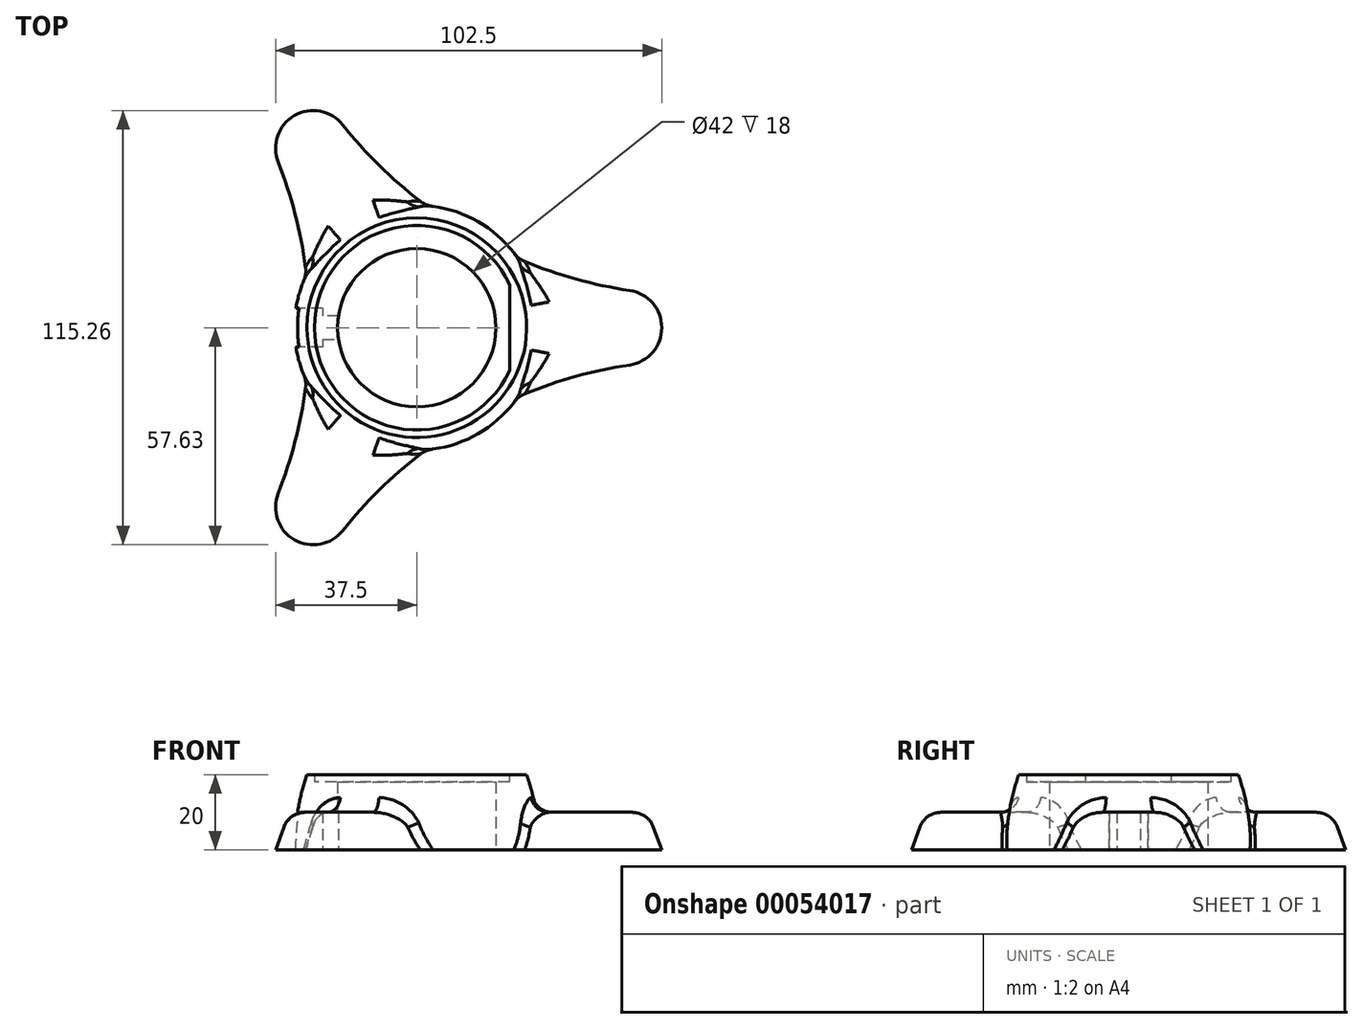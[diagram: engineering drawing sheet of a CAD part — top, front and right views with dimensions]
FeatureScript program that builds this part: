
annotation { "Feature Type Name" : "Feature", "Feature Type Description" : "" }
export const myFeature = defineFeature(function(context is Context, id is Id, definition is map)
    precondition{}
    {
        {
            var Q0;
            Q0=qCreatedBy(makeId("Front.planeOp"),FACE);
            var sketch = newSketch(context, id + "F0", { "sketchPlane" : qUnion([Q0])});
            skLineSegment(sketch, "E0", {"start": v(21, 0) * mm, "end": v(21, 18) * mm});
            skLineSegment(sketch, "E1", {"start": v(21, 18) * mm, "end": v(27.15, 18) * mm});
            skLineSegment(sketch, "E2", {"start": v(27.15, 18) * mm, "end": v(27.15, 20) * mm});
            skLineSegment(sketch, "E3", {"start": v(27.15, 20) * mm, "end": v(29.15, 20) * mm});
            skLineSegment(sketch, "E4", {"start": v(21, 0) * mm, "end": v(32.5, 0) * mm});
            skArc(sketch, "E5", {"start": v(32.5, 0) * mm, "mid": v(31.66, 10.14) * mm, "end": v(29.15, 20) * mm});
            skLineSegment(sketch, "E6", {"start": v(0, 0) * mm, "end": v(0, 24.17) * mm, "construction": true});
            skSolve(sketch);
        }
        {
            var Q0;
            Q0 = qSketchRegion(id + "F0", true);
            var Q1;
            Q1=sQuery(id+"F0.wireOp",EDGE,"E6");
            revolve(context, id + "F1", {"entities" : qUnion([Q0]), "axis" : qUnion([Q1]), "revolveType" : RevolveType.FULL});
        }
        {
            var Q0;
            Q0=qCreatedBy(makeId("Top.planeOp"),FACE);
            var sketch = newSketch(context, id + "F2", { "sketchPlane" : qUnion([Q0])});
            skLineSegment(sketch, "E7", {"start": v(0, 0) * mm, "end": v(55, 0) * mm, "construction": true});
            skLineSegment(sketch, "E8", {"start": v(0, 0) * mm, "end": v(-27.5, -47.63) * mm, "construction": true});
            skLineSegment(sketch, "E9", {"start": v(0, 0) * mm, "end": v(-27.5, 47.63) * mm, "construction": true});
            skArc(sketch, "E10", {"start": v(56.48, -9.89) * mm, "mid": v(65, 0) * mm, "end": v(56.48, 9.89) * mm});
            skArc(sketch, "E11", {"start": v(-36.8, -43.97) * mm, "mid": v(-32.5, -56.3) * mm, "end": v(-19.67, -53.86) * mm});
            skArc(sketch, "E12", {"start": v(-19.67, 53.86) * mm, "mid": v(-32.5, 56.3) * mm, "end": v(-36.8, 43.97) * mm});
            skArc(sketch, "E13", {"start": v(56.48, -9.89) * mm, "mid": v(14.23, -24.65) * mm, "end": v(-19.67, -53.86) * mm});
            skArc(sketch, "E14", {"start": v(-36.8, -43.97) * mm, "mid": v(-28.46, 0) * mm, "end": v(-36.8, 43.97) * mm});
            skArc(sketch, "E15", {"start": v(-19.67, 53.86) * mm, "mid": v(14.23, 24.65) * mm, "end": v(56.48, 9.89) * mm});
            skCircle(sketch, "E16", {"center": v(0, 0) * mm, "radius": 21 * mm});
            skSolve(sketch);
        }
        {
            var Q0;
            Q0 = qSketchRegion(id + "F2", true);
            extrude(context, id + "F3", {"entities" : qUnion([Q0]), "operationType" : NewBodyOperationType.ADD, "depth" : 10 * mm, "hasDraft" : true, "draftAngle" : 20 * degree, "draftPullDirection" : true});
        }
        {
            var Q0;
            {var subQ0=sQuery(id+"F2.wireOp",EDGE,"E13");var subQ1=sQuery(id+"F2.wireOp",EDGE,"E11");Q0=makeQuery(id+"F3.boolean.opBoolean","SPLIT",EDGE,{"disambiguationData":[TD([makeQuery(id+"F3.opExtrude","SWEPT_FACE",FACE,{"disambiguationData":[OSD([subQ1])]})])],"derivedFrom":makeQuery(id+"F3.opExtrude","CAP_EDGE",EDGE,{"disambiguationData":[OSD([subQ0])],"isStart":false})});}
            var Q1;
            {var subQ0=sQuery(id+"F2.wireOp",EDGE,"E10");var subQ1=sQuery(id+"F2.wireOp",EDGE,"E13");Q1=makeQuery(id+"F3.boolean.opBoolean","SPLIT",EDGE,{"disambiguationData":[TD([makeQuery(id+"F3.opExtrude","SWEPT_FACE",FACE,{"disambiguationData":[OSD([subQ0])]})])],"derivedFrom":makeQuery(id+"F3.opExtrude","CAP_EDGE",EDGE,{"disambiguationData":[OSD([subQ1])],"isStart":false})});}
            var Q2;
            Q2=makeQuery(id+"F3.opExtrude","CAP_EDGE",EDGE,{"disambiguationData":[OSD([sQuery(id+"F2.wireOp",EDGE,"E12")])],"isStart":false});
            fillet(context, id + "F4", {"entities" : qUnion([Q0, Q1, Q2]), "radius" : 6 * mm, "tangentPropagation" : true, "allowEdgeOverflow" : false});
        }
        {
            var Q0;
            Q0=makeQuery(id+"F1.opRevolve","SWEPT_FACE",FACE,{"disambiguationData":[OSD([sQuery(id+"F0.wireOp",EDGE,"E3")])]});
            var sketch = newSketch(context, id + "F5", { "sketchPlane" : qUnion([Q0])});
            skArc(sketch, "E17", {"start": v(24.65, -11.38) * mm, "mid": v(27.15, 0) * mm, "end": v(24.65, 11.38) * mm});
            skLineSegment(sketch, "E18", {"start": v(24.65, 11.38) * mm, "end": v(24.65, -11.38) * mm});
            skCircle(sketch, "E19", {"center": v(-23.45, 0) * mm, "radius": 1.25 * mm, "construction": true});
            skCircle(sketch, "E20", {"center": v(0, 0) * mm, "radius": 26.65 * mm, "construction": true});
            skCircle(sketch, "E21.1.0", {"center": v(11.72, -20.3) * mm, "radius": 1.25 * mm, "construction": true});
            skCircle(sketch, "E21.2.0", {"center": v(11.72, 20.3) * mm, "radius": 1.25 * mm, "construction": true});
            skSolve(sketch);
        }
        {
            var Q0;
            Q0 = qSketchRegion(id + "F5", true);
            var Q1;
            Q1=makeQuery(id+"F1.opRevolve","SWEPT_BODY",BODY,{"disambiguationData":[OSD([sQuery(id+"F0.wireOp",EDGE,"6pkRBRF0-ryt5-2erR-Cuzx-a48DatGhJrHf"),sQuery(id+"F0.wireOp",EDGE,"E0"),sQuery(id+"F0.wireOp",EDGE,"E1"),sQuery(id+"F0.wireOp",EDGE,"E2"),sQuery(id+"F0.wireOp",EDGE,"E3"),sQuery(id+"F0.wireOp",EDGE,"DangXWH5-A3Qb-kWuE-QbsE-42BrN12sU1pv"),sQuery(id+"F0.wireOp",EDGE,"E4"),sQuery(id+"F0.wireOp",EDGE,"E5")])]});
            extrude(context, id + "F6", {"entities" : qUnion([Q0]), "operationType" : NewBodyOperationType.ADD, "endBound" : BoundingType.UP_TO_BODY, "oppositeDirection" : true, "endBoundEntityBody" : qUnion([Q1]), "depth" : 25 * mm});
        }
        {
            var Q0;
            Q0=qCreatedBy(makeId("Top.planeOp"),FACE);
            var sketch = newSketch(context, id + "F7", { "sketchPlane" : qUnion([Q0])});
            skLineSegment(sketch, "E22.bottom", {"start": v(-25, -5.1) * mm, "end": v(-32.5, -5.1) * mm});
            skLineSegment(sketch, "E22.top", {"start": v(-25, 5.1) * mm, "end": v(-32.5, 5.1) * mm});
            skLineSegment(sketch, "E22.right", {"start": v(-32.5, -5.1) * mm, "end": v(-32.5, 5.1) * mm});
            skLineSegment(sketch, "E23", {"start": v(-25, -3.1) * mm, "end": v(-25, -5.1) * mm});
            skLineSegment(sketch, "E24", {"start": v(-25, -3.1) * mm, "end": v(-20.77, -3.1) * mm});
            skLineSegment(sketch, "E25", {"start": v(-20.77, -3.1) * mm, "end": v(-20.77, 3.1) * mm});
            skLineSegment(sketch, "E26", {"start": v(-20.77, 3.1) * mm, "end": v(-25, 3.1) * mm});
            skLineSegment(sketch, "E27", {"start": v(-25, 5.1) * mm, "end": v(-25, 3.1) * mm});
            skSolve(sketch);
        }
        {
            var Q0;
            Q0 = qSketchRegion(id + "F7", true);
            extrude(context, id + "F8", {"entities" : qUnion([Q0]), "operationType" : NewBodyOperationType.REMOVE, "depth" : 10.2 * mm});
        }
        {
            var Q0;
            Q0=makeQuery(id+"F3.boolean.opBoolean","INTERSECT",EDGE,{"disambiguationData":[OD(1.0)],"derivedFrom":[makeQuery(id+"F1.opRevolve","SWEPT_FACE",FACE,{"disambiguationData":[OSD([sQuery(id+"F0.wireOp",EDGE,"E5")])]}),makeQuery(id+"F3.opExtrude","SWEPT_FACE",FACE,{"disambiguationData":[OSD([sQuery(id+"F2.wireOp",EDGE,"E14")])]})]});
            var Q1;
            Q1=makeQuery(id+"F3.boolean.opBoolean","INTERSECT",EDGE,{"disambiguationData":[OD(0.0)],"derivedFrom":[makeQuery(id+"F1.opRevolve","SWEPT_FACE",FACE,{"disambiguationData":[OSD([sQuery(id+"F0.wireOp",EDGE,"E5")])]}),makeQuery(id+"F3.opExtrude","SWEPT_FACE",FACE,{"disambiguationData":[OSD([sQuery(id+"F2.wireOp",EDGE,"E14")])]})]});
            var Q2;
            Q2=makeQuery(id+"F3.boolean.opBoolean","INTERSECT",EDGE,{"disambiguationData":[OD(0.0)],"derivedFrom":[makeQuery(id+"F1.opRevolve","SWEPT_FACE",FACE,{"disambiguationData":[OSD([sQuery(id+"F0.wireOp",EDGE,"E5")])]}),makeQuery(id+"F3.opExtrude","SWEPT_FACE",FACE,{"disambiguationData":[OSD([sQuery(id+"F2.wireOp",EDGE,"E13")])]})]});
            fillet(context, id + "F9", {"entities" : qUnion([Q0, Q1, Q2]), "radius" : 5 * mm, "tangentPropagation" : true, "allowEdgeOverflow" : false});
        }
    });
